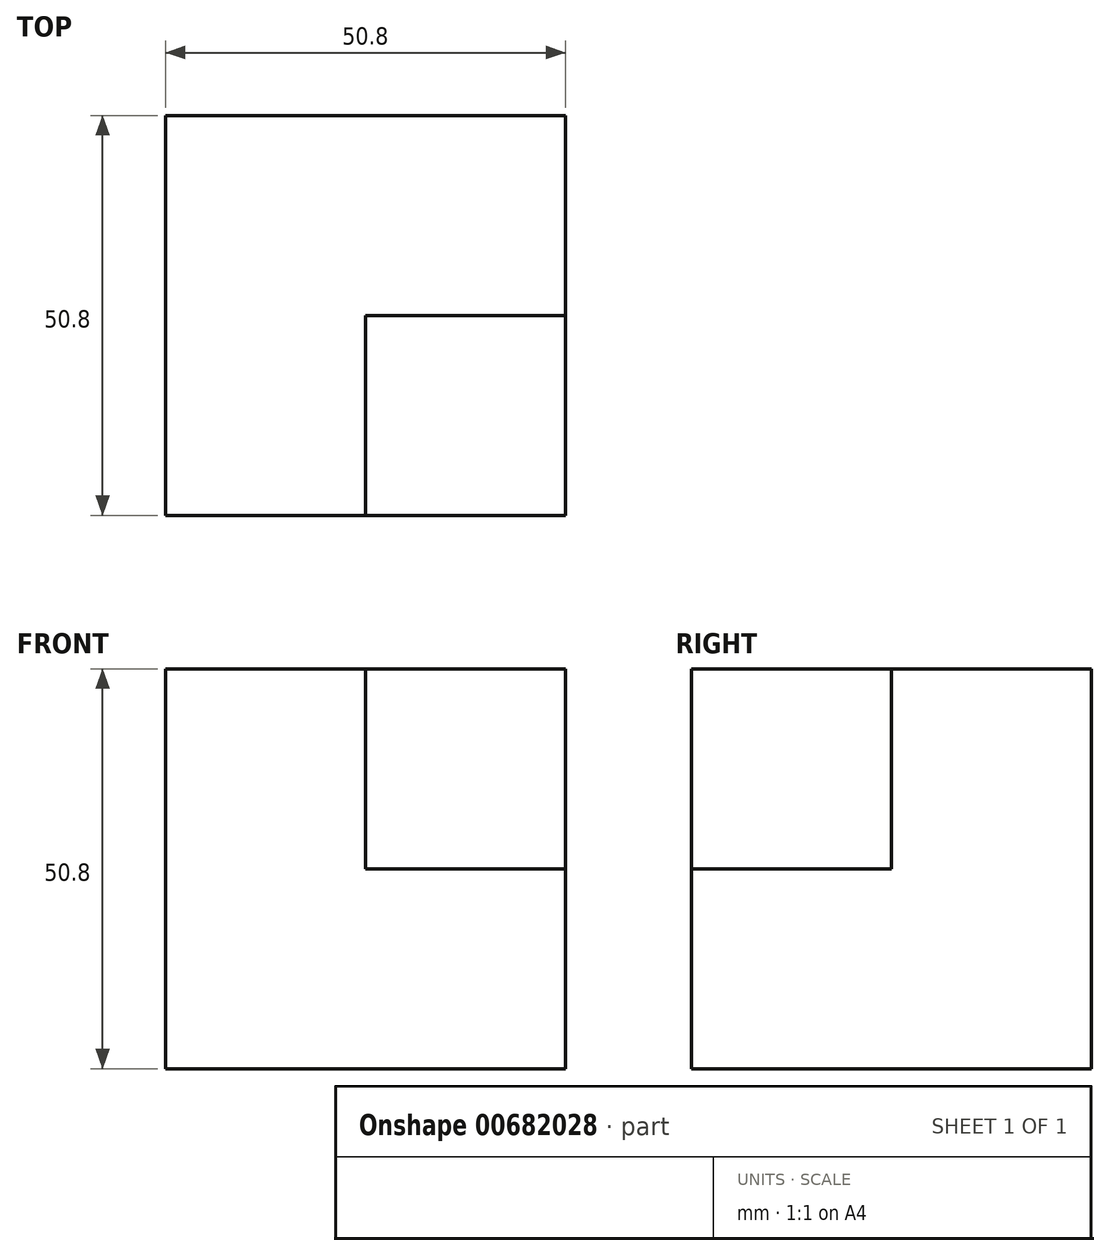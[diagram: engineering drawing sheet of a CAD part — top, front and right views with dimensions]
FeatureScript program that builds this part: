
annotation { "Feature Type Name" : "Feature", "Feature Type Description" : "" }
export const myFeature = defineFeature(function(context is Context, id is Id, definition is map)
    precondition{}
    {
        {
            var Q0;
            Q0=qCreatedBy(makeId("Front.planeOp"),FACE);
            var sketch = newSketch(context, id + "F0", { "sketchPlane" : qUnion([Q0])});
            skLineSegment(sketch, "E0", {"start": v(-43.8, 42.3) * mm, "end": v(-43.8, -8.5) * mm});
            skLineSegment(sketch, "E1", {"start": v(-43.8, -8.5) * mm, "end": v(7, -8.5) * mm});
            skLineSegment(sketch, "E2", {"start": v(7, -8.5) * mm, "end": v(7, 42.3) * mm});
            skLineSegment(sketch, "E3", {"start": v(7, 42.3) * mm, "end": v(-43.8, 42.3) * mm});
            skSolve(sketch);
        }
        {
            var Q0;
            Q0 = qSketchRegion(id + "F0", true);
            extrude(context, id + "F1", {"entities" : qUnion([Q0]), "depth" : 50.8 * mm, "offsetDistance" : 25.4 * mm});
        }
        {
            var Q0;
            Q0=makeQuery(id+"F1.opExtrude","CAP_FACE",FACE,{"disambiguationData":[OSD([sQuery(id+"F0.wireOp",EDGE,"E0"),sQuery(id+"F0.wireOp",EDGE,"E1"),sQuery(id+"F0.wireOp",EDGE,"E2"),sQuery(id+"F0.wireOp",EDGE,"E3")])],"isStart":false});
            var sketch = newSketch(context, id + "F2", { "sketchPlane" : qUnion([Q0])});
            skLineSegment(sketch, "E4.bottom", {"start": v(7, 42.3) * mm, "end": v(-18.4, 42.3) * mm});
            skLineSegment(sketch, "E4.top", {"start": v(7, 16.9) * mm, "end": v(-18.4, 16.9) * mm});
            skLineSegment(sketch, "E4.left", {"start": v(7, 42.3) * mm, "end": v(7, 16.9) * mm});
            skLineSegment(sketch, "E4.right", {"start": v(-18.4, 42.3) * mm, "end": v(-18.4, 16.9) * mm});
            skSolve(sketch);
        }
        {
            var Q0;
            Q0 = qSketchRegion(id + "F2", true);
            extrude(context, id + "F3", {"entities" : qUnion([Q0]), "operationType" : NewBodyOperationType.REMOVE, "oppositeDirection" : true, "depth" : 25.4 * mm, "offsetDistance" : 25.4 * mm});
        }
    });
